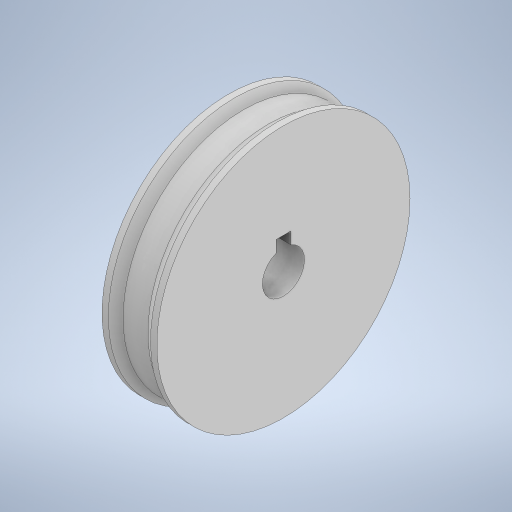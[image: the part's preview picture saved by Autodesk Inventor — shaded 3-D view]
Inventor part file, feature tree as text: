
AUTODESK INVENTOR PART (.ipt)
format: ipt  version: 2024 (Build 280153000, 153)  size: 254,976 bytes
history: native  units: mm
features: thicken_offset x2, sketch x2, other x1, revolve x1, extrude x1
ambient origin geometry x8: Origin, YZ Plane, XZ Plane, XY Plane, X Axis, Y Axis, Z Axis, Center Point
bodies: Body1 (feature_tree)
feature tree (7):
  other  "POLEA"
  revolve  "Revolution1"  Angle=90.0deg
  thicken_offset  "Thicken1"
  thicken_offset  "Thicken2"
  extrude  "Extrusion1"  Depth=3.0mm
  sketch  "Sketch1"  dims[d3=10.0mm d6=90.0deg]
  sketch  "Sketch2"  dims[d7=3.0mm d8=3.0mm d9=3.0mm d10=3.0mm d11=7.0mm d12=10.0mm d13=0.0mm d14=0.0mm]
